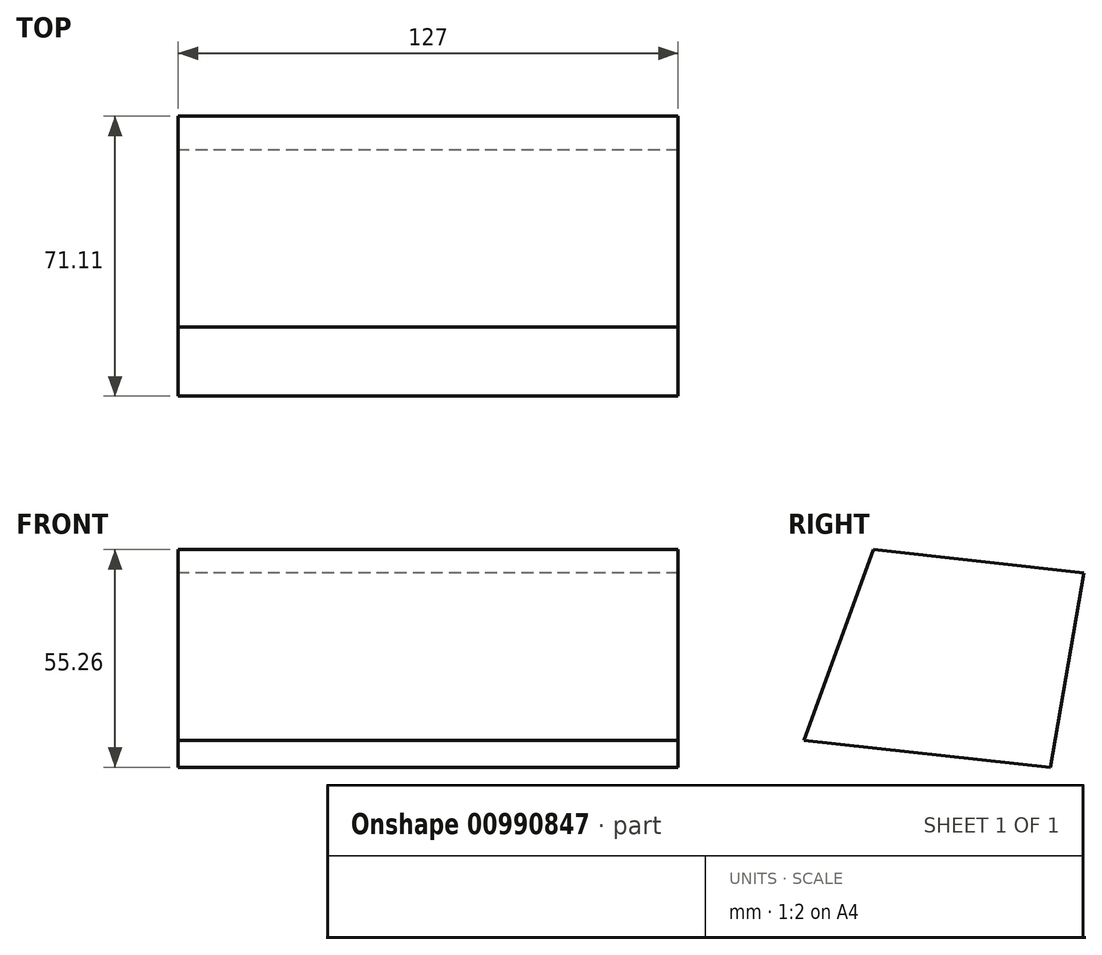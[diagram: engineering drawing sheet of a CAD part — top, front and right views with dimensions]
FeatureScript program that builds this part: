
annotation { "Feature Type Name" : "Feature", "Feature Type Description" : "" }
export const myFeature = defineFeature(function(context is Context, id is Id, definition is map)
    precondition{}
    {
        {
            var Q0;
            Q0=qCreatedBy(makeId("Right.planeOp"),FACE);
            var sketch = newSketch(context, id + "F0", { "sketchPlane" : qUnion([Q0])});
            skLineSegment(sketch, "E0", {"start": v(-31.56, -20.99) * mm, "end": v(30.98, -27.84) * mm});
            skLineSegment(sketch, "E1", {"start": v(30.98, -27.84) * mm, "end": v(39.55, 21.56) * mm});
            skLineSegment(sketch, "E2", {"start": v(39.55, 21.56) * mm, "end": v(-13.93, 27.42) * mm});
            skLineSegment(sketch, "E3", {"start": v(-13.93, 27.42) * mm, "end": v(-31.56, -20.99) * mm});
            skSolve(sketch);
        }
        {
            var Q0;
            Q0 = qSketchRegion(id + "F0", true);
            extrude(context, id + "F1", {"entities" : qUnion([Q0]), "depth" : 127 * mm, "offsetDistance" : 25.4 * mm});
        }
    });
